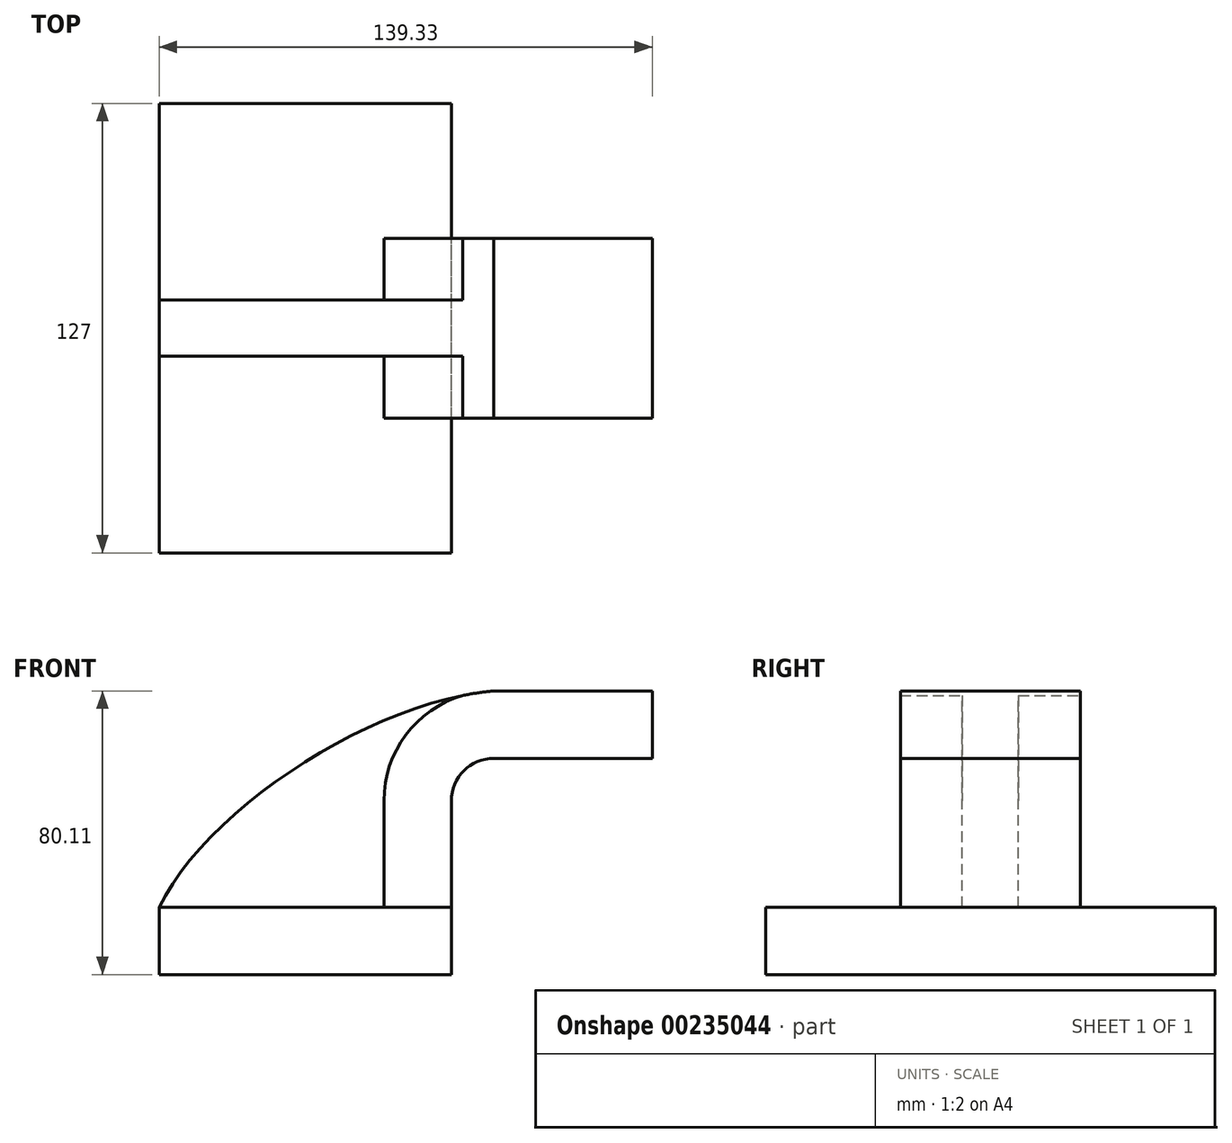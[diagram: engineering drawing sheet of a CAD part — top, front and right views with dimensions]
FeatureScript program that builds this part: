
annotation { "Feature Type Name" : "Feature", "Feature Type Description" : "" }
export const myFeature = defineFeature(function(context is Context, id is Id, definition is map)
    precondition{}
    {
        {
            var Q0;
            Q0=qCreatedBy(makeId("Front.planeOp"),FACE);
            var sketch = newSketch(context, id + "F0", { "sketchPlane" : qUnion([Q0])});
            skLineSegment(sketch, "E0.bottom", {"start": v(-41.28, 9.52) * mm, "end": v(41.28, 9.53) * mm});
            skLineSegment(sketch, "E0.top", {"start": v(-41.28, -9.53) * mm, "end": v(41.28, -9.53) * mm});
            skLineSegment(sketch, "E0.left", {"start": v(-41.28, 9.52) * mm, "end": v(-41.28, -9.53) * mm});
            skLineSegment(sketch, "E0.right", {"start": v(41.28, 9.53) * mm, "end": v(41.28, -9.52) * mm});
            skPoint(sketch, "E0.middle", {"position": v(0, 0) * mm});
            skLineSegment(sketch, "E1.bottom", {"start": v(72.65, 38.54) * mm, "end": v(123.45, 38.54) * mm});
            skLineSegment(sketch, "E1.top", {"start": v(72.65, 67.11) * mm, "end": v(123.45, 67.11) * mm});
            skLineSegment(sketch, "E1.left", {"start": v(72.65, 38.54) * mm, "end": v(72.65, 67.11) * mm});
            skLineSegment(sketch, "E1.right", {"start": v(123.45, 38.54) * mm, "end": v(123.45, 67.11) * mm});
            skPoint(sketch, "E1.middle", {"position": v(98.05, 52.83) * mm});
            skLineSegment(sketch, "E2", {"start": v(41.27, 9.53) * mm, "end": v(41.27, 39.52) * mm});
            skArc(sketch, "E3", {"start": v(41.28, 39.52) * mm, "mid": v(44.8, 48.01) * mm, "end": v(53.28, 51.53) * mm});
            skLineSegment(sketch, "E4", {"start": v(53.28, 51.53) * mm, "end": v(98.05, 51.53) * mm});
            skPoint(sketch, "E4.endSnap0", {"position": v(98.05, 38.54) * mm});
            skLineSegment(sketch, "E5.0", {"start": v(53.28, 70.58) * mm, "end": v(98.05, 70.58) * mm});
            skArc(sketch, "E5.1", {"start": v(22.23, 39.52) * mm, "mid": v(31.32, 61.48) * mm, "end": v(53.28, 70.58) * mm});
            skLineSegment(sketch, "E5.2", {"start": v(22.22, 9.53) * mm, "end": v(22.22, 39.52) * mm});
            skLineSegment(sketch, "E6", {"start": v(98.05, 51.53) * mm, "end": v(98.05, 70.58) * mm});
            skFitSpline(sketch, "E7", {"points": [v(-41.28, 9.52) * mm, v(53.28, 70.58) * mm], "startDerivative": vector(39.88, 82.29) * mm, "endDerivative": vector(104.8, 8.95) * mm});
            skSolve(sketch);
        }
        {
            var Q0;
            Q0=makeQuery(id+"F0.imprint","IMPRINT",FACE,{"disambiguationData":[TD([[makeQuery(id+"F0.imprint","IMPRINT",EDGE,{"derivedFrom":sQuery(id+"F0.wireOp",EDGE,"E0.top")}),1.0]])]});
            extrude(context, id + "F1", {"entities" : qUnion([Q0]), "endBound" : BoundingType.SYMMETRIC, "depth" : 127 * mm});
        }
        {
            var Q0;
            {var subQ9=sQuery(id+"F0.wireOp",EDGE,"E2");Q0=makeQuery(id+"F0.imprint","IMPRINT",FACE,{"disambiguationData":[TD([[makeQuery(id+"F0.imprint","IMPRINT",EDGE,{"derivedFrom":subQ9}),1.0]])]});}
            var Q1;
            {var subQ0=sQuery(id+"F0.wireOp",EDGE,"E1.left");var subQ1=sQuery(id+"F0.wireOp",EDGE,"E1.top");var subQ2=makeQuery(id+"F0.imprint","INTERSECT",VERTEX,{"derivedFrom":[subQ1,subQ0]});Q1=makeQuery(id+"F0.imprint","IMPRINT",FACE,{"disambiguationData":[TD([[makeQuery(id+"F0.imprint","IMPRINT",EDGE,{"disambiguationData":[TD([[subQ2,-1.0]])],"derivedFrom":subQ1}),-1.0]])]});}
            extrude(context, id + "F2", {"entities" : qUnion([Q0, Q1]), "operationType" : NewBodyOperationType.ADD, "endBound" : BoundingType.SYMMETRIC, "depth" : 50.8 * mm});
        }
        {
            var Q0;
            {var subQ3=sQuery(id+"F0.wireOp",EDGE,"E5.2");Q0=makeQuery(id+"F0.imprint","IMPRINT",FACE,{"disambiguationData":[TD([[makeQuery(id+"F0.imprint","IMPRINT",EDGE,{"derivedFrom":subQ3}),1.0]])]});}
            extrude(context, id + "F3", {"entities" : qUnion([Q0]), "operationType" : NewBodyOperationType.ADD, "endBound" : BoundingType.SYMMETRIC, "depth" : 15.88 * mm});
        }
        {
            var Q0;
            Q0=makeQuery(id+"F0.imprint","IMPRINT",FACE,{"disambiguationData":[TD([[makeQuery(id+"F0.imprint","IMPRINT",EDGE,{"derivedFrom":sQuery(id+"F0.wireOp",EDGE,"E0.top")}),1.0]])]});
            extrude(context, id + "F4", {"entities" : qUnion([Q0]), "endBound" : BoundingType.SYMMETRIC, "depth" : 127 * mm});
        }
    });
